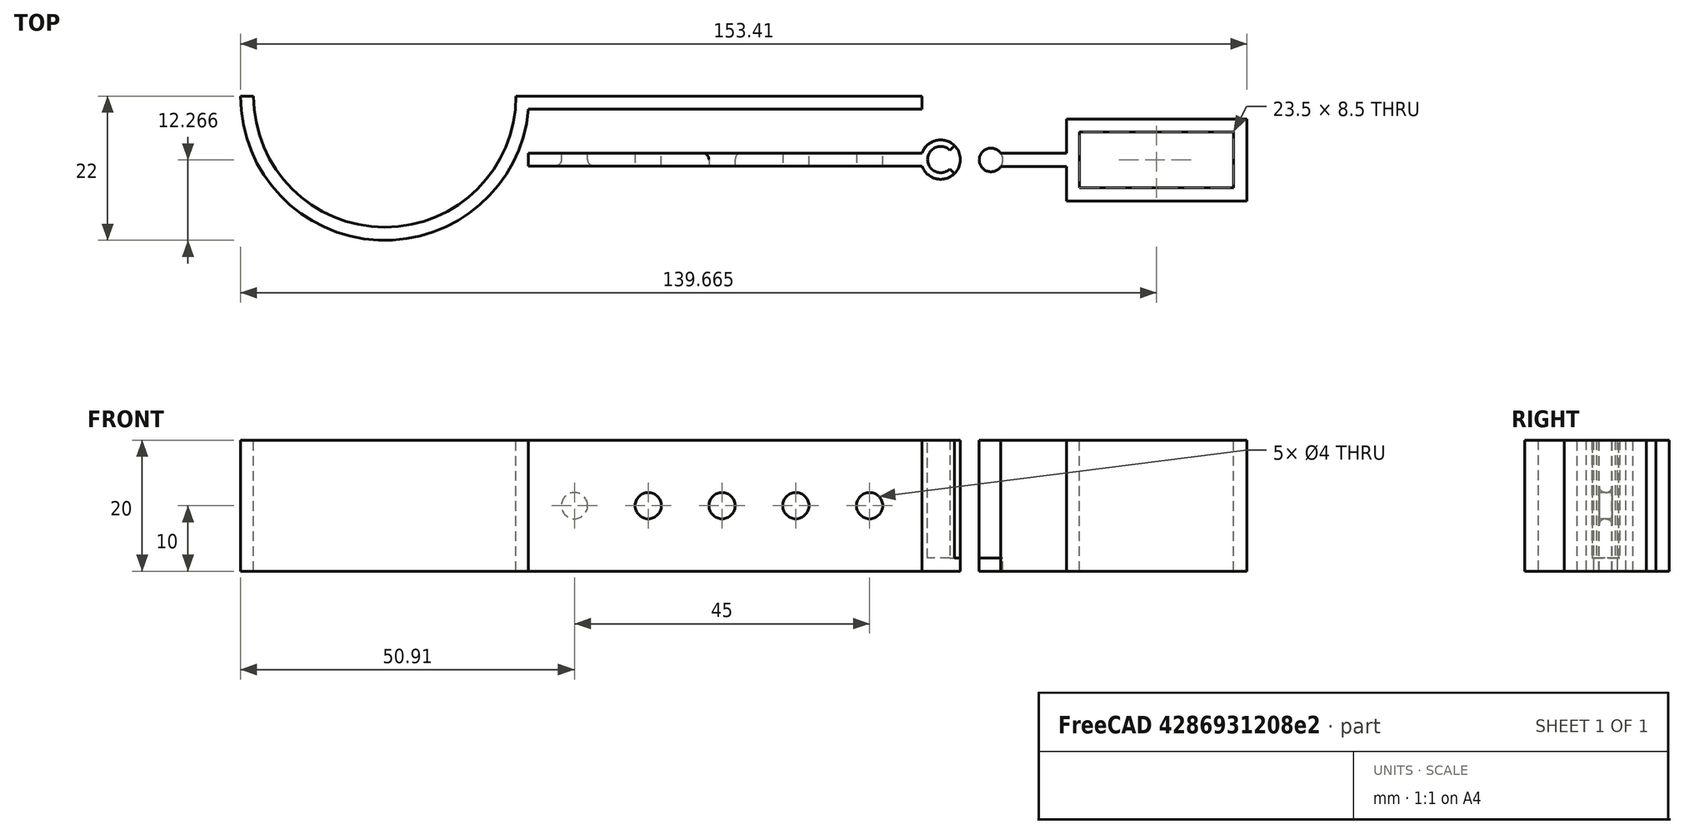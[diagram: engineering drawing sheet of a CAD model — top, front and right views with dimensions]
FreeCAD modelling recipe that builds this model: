
FCSTD DOCUMENT  (FreeCAD 0.16R6712 (Git))
Label: Porte webcam
License: All rights reserved
LicenseURL: http://en.wikipedia.org/wiki/All_rights_reserved
objects: Sketcher::SketchObject×7, PartDesign::Pocket×4, PartDesign::Pad×3, Mesh::Feature×3, PartDesign::LinearPattern×2, PartDesign::Fillet×2
note: 25 computed .brp shape members not serialized (recipe doc carries the construction recipe); baked Part::Feature solids carry a one-line shape summary decoded from their .brp

FEATURE [Sketcher::SketchObject] Sketch
  sketch-geometry (6):
    g0: ArcOfCircle CenterX=-81.9089 CenterY=0 CenterZ=0 NormalX=0 NormalY=0 NormalZ=1 Radius=20 StartAngle=3.14159 EndAngle=6.28319
    g1: ArcOfCircle CenterX=-81.9089 CenterY=0 CenterZ=0 NormalX=0 NormalY=0 NormalZ=1 Radius=22 StartAngle=3.14159 EndAngle=6.19215
    g2: LineSegment StartX=-60 StartY=-2 StartZ=0 EndX=0 EndY=-2 EndZ=0
    g3: LineSegment StartX=-61.9089 StartY=0 StartZ=0 EndX=0 EndY=0 EndZ=0
    g4: LineSegment StartX=0 StartY=-2 StartZ=0 EndX=0 EndY=0 EndZ=0
    g5: LineSegment StartX=-103.909 StartY=0 StartZ=0 EndX=-101.909 EndY=0 EndZ=0
  constraints (18):
    c: PointOnObject(g0,g-1)
    c: PointOnObject(g0,g-1)
    c: PointOnObject(g0,g-1)
    c: Radius(g0) = 20
    c: Coincident(g1,g0)
    c: PointOnObject(g1,g-1)
    c: DistanceX(g1,g0) = 2
    c: Coincident(g2,g1)
    c: Horizontal(g2)
    c: Coincident(g3,g-1)
    c: DistanceY(g2,g-1) = 2
    c: Coincident(g4,g-1)
    c: Vertical(g4)
    c: Coincident(g2,g4)
    c: Coincident(g3,g0)
    c: Coincident(g5,g1)
    c: Coincident(g5,g0)
    c: DistanceX(g1,g2) = 60
FEATURE [PartDesign::Pad] Pad
  Length = 20
  Length2 = 100
  Sketch = -> Sketch
  Type = 0
FEATURE [Sketcher::SketchObject] Sketch001
  ExternalGeometry = -> [Pad]
  Placement = pos=(0,-2,0) rot=(1,0,0;1.5708rad)
  Support = -> Pad [Face5]
  sketch-geometry (3):
    g0: Circle CenterX=-53 CenterY=10 CenterZ=0 NormalX=0 NormalY=0 NormalZ=1 Radius=2
    g1: LineSegment [constr] StartX=-53 StartY=10 StartZ=0 EndX=-53 EndY=20 EndZ=0
    g2: LineSegment [constr] StartX=-53 StartY=10 StartZ=0 EndX=-53 EndY=0 EndZ=0
  constraints (9):
    c: Radius(g0) = 2
    c: DistanceX(g-3,g0) = 7
    c: Coincident(g1,g0)
    c: Vertical(g1)
    c: Coincident(g2,g0)
    c: PointOnObject(g2,g-4)
    c: Vertical(g2)
    c: PointOnObject(g1,g-3)
    c: Equal(g1,g2)
FEATURE [PartDesign::Pocket] Pocket
  Length = 5
  Sketch = -> Sketch001
  Type = 1
FEATURE [Sketcher::SketchObject] Sketch002
  sketch-geometry (4):
    g0: LineSegment StartX=0 StartY=-8.67651 StartZ=0 EndX=-60 EndY=-8.67651 EndZ=0
    g1: LineSegment StartX=-60 StartY=-8.67651 StartZ=0 EndX=-60 EndY=-10.6765 EndZ=0
    g2: LineSegment StartX=-60 StartY=-10.6765 StartZ=0 EndX=0 EndY=-10.6765 EndZ=0
    g3: ArcOfCircle CenterX=2.82843 CenterY=-9.67651 CenterZ=0 NormalX=0 NormalY=0 NormalZ=1 Radius=3 StartAngle=3.48143 EndAngle=9.08494
  constraints (12):
    c: PointOnObject(g0,g-2)
    c: Horizontal(g0)
    c: Coincident(g0,g1)
    c: Vertical(g1)
    c: Coincident(g1,g2)
    c: PointOnObject(g2,g-2)
    c: Horizontal(g2)
    c: DistanceY(g1,g0) = 2
    c: DistanceX(g1,g2) = 60
    c: Coincident(g3,g0)
    c: Coincident(g3,g2)
    c: Radius(g3) = 3
FEATURE [PartDesign::Pad] Pad001
  Length = 20
  Length2 = 100
  Sketch = -> Sketch002
  Type = 0
FEATURE [Sketcher::SketchObject] Sketch003
  ExternalGeometry = -> [Pad001]
  Placement = pos=(0,-10.6765,0) rot=(1,0,0;1.5708rad)
  Support = -> Pad001 [Face3]
  sketch-geometry (3):
    g0: LineSegment [constr] StartX=-53 StartY=10 StartZ=0 EndX=-53 EndY=20 EndZ=0
    g1: LineSegment [constr] StartX=-53 StartY=10 StartZ=0 EndX=-53 EndY=0 EndZ=0
    g2: Circle CenterX=-53 CenterY=10 CenterZ=0 NormalX=0 NormalY=0 NormalZ=1 Radius=2
  constraints (9):
    c: PointOnObject(g0,g-3)
    c: Vertical(g0)
    c: PointOnObject(g1,g-4)
    c: Vertical(g1)
    c: Equal(g1,g0)
    c: Radius(g2) = 2
    c: Coincident(g1,g2)
    c: Coincident(g1,g0)
    c: DistanceX(g-3,g0) = 7
FEATURE [PartDesign::Pocket] Pocket001
  Length = 5
  Sketch = -> Sketch003
  Type = 1
FEATURE [Sketcher::SketchObject] Sketch004
  sketch-geometry (14):
    g0: LineSegment StartX=24.0046 StartY=-5.48438 StartZ=0 EndX=47.5046 EndY=-5.48438 EndZ=0
    g1: LineSegment StartX=47.5046 StartY=-5.48438 StartZ=0 EndX=47.5046 EndY=-13.9844 EndZ=0
    g2: LineSegment StartX=47.5046 StartY=-13.9844 StartZ=0 EndX=24.0046 EndY=-13.9844 EndZ=0
    g3: LineSegment StartX=24.0046 StartY=-13.9844 StartZ=0 EndX=24.0046 EndY=-5.48438 EndZ=0
    g4: LineSegment StartX=22.0046 StartY=-3.48438 StartZ=0 EndX=49.5046 EndY=-3.48438 EndZ=0
    g5: LineSegment StartX=49.5046 StartY=-3.48438 StartZ=0 EndX=49.5046 EndY=-15.9844 EndZ=0
    g6: LineSegment StartX=49.5046 StartY=-15.9844 StartZ=0 EndX=22.0046 EndY=-15.9844 EndZ=0
    g7: LineSegment StartX=12.0046 StartY=-8.73438 StartZ=0 EndX=22.0046 EndY=-8.73438 EndZ=0
    g8: LineSegment StartX=22.0046 StartY=-10.7344 StartZ=0 EndX=12.0046 EndY=-10.7344 EndZ=0
    g9: LineSegment StartX=22.0046 StartY=-15.9844 StartZ=0 EndX=22.0046 EndY=-10.7344 EndZ=0
    g10: LineSegment StartX=22.0046 StartY=-8.73438 StartZ=0 EndX=22.0046 EndY=-3.48438 EndZ=0
    g11: ArcOfCircle CenterX=10.508 CenterY=-9.73438 CenterZ=0 NormalX=0 NormalY=0 NormalZ=1 Radius=1.8 StartAngle=0.589031 EndAngle=5.69415
    g12: LineSegment [constr] StartX=12.0046 StartY=-10.7344 StartZ=0 EndX=10.508 EndY=-9.73438 EndZ=0
    g13: LineSegment [constr] StartX=10.508 StartY=-9.73438 StartZ=0 EndX=12.0046 EndY=-8.73438 EndZ=0
  constraints (39):
    c: Coincident(g0,g1)
    c: Coincident(g1,g2)
    c: Coincident(g2,g3)
    c: Coincident(g3,g0)
    c: Horizontal(g0)
    c: Horizontal(g2)
    c: Vertical(g1)
    c: Vertical(g3)
    c: Coincident(g4,g5)
    c: Coincident(g5,g6)
    c: Horizontal(g4)
    c: Horizontal(g6)
    c: Vertical(g5)
    c: DistanceY(g5,g1) = 2
    c: DistanceX(g1,g5) = 2
    c: DistanceX(g4,g0) = 2
    c: DistanceY(g0,g4) = 2
    c: DistanceX(g0,g0) = 23.5
    c: DistanceY(g2,g0) = 8.5
    c: Horizontal(g7)
    c: Horizontal(g8)
    c: DistanceY(g8,g7) = 2
    c: Coincident(g9,g6)
    c: Vertical(g9)
    c: Coincident(g10,g7)
    c: Coincident(g10,g4)
    c: Vertical(g10)
    c: Equal(g9,g10)
    c: Coincident(g9,g8)
    c: DistanceX(g6,g2) = 2
    c: DistanceX(g8,g8) = 10
    c: Coincident(g11,g7)
    c: Coincident(g11,g8)
    c: Radius(g11) = 1.8
    c: Coincident(g12,g8)
    c: Coincident(g12,g11)
    c: Coincident(g13,g11)
    c: Coincident(g13,g7)
    c: Equal(g8,g7)
FEATURE [PartDesign::LinearPattern] LinearPattern
  Direction = -> Sketch001 [H_Axis]
  Length = 45
  Occurrences = 5
  Originals = -> [Pocket]
FEATURE [PartDesign::Pad] Pad002
  Length = 20
  Length2 = 100
  Sketch = -> Sketch004
  Type = 0
FEATURE [PartDesign::LinearPattern] LinearPattern001
  Direction = -> Sketch003 [H_Axis]
  Length = 45
  Occurrences = 5
  Originals = -> [Pocket001]
FEATURE [Sketcher::SketchObject] Sketch005
  ExternalGeometry = -> [LinearPattern001]
  Placement = pos=(0,0,20) rot=(0,0,1;0rad)
  Support = -> LinearPattern001 [Face4]
  sketch-geometry (5):
    g0: ArcOfCircle CenterX=2.82843 CenterY=-9.67651 CenterZ=0 NormalX=0 NormalY=0 NormalZ=1 Radius=3.81642 StartAngle=5.49779 EndAngle=7.06858
    g1: LineSegment [constr] StartX=2.82843 StartY=-9.67651 StartZ=0 EndX=7.82755 EndY=-9.67651 EndZ=0
    g2: ArcOfCircle CenterX=2.82843 CenterY=-9.67651 CenterZ=0 NormalX=0 NormalY=0 NormalZ=1 Radius=2 StartAngle=0.785398 EndAngle=5.49779
    g3: LineSegment StartX=4.24264 StartY=-8.26229 StartZ=0 EndX=5.52704 EndY=-6.97789 EndZ=0
    g4: LineSegment StartX=4.24264 StartY=-11.0907 StartZ=0 EndX=5.52704 EndY=-12.3751 EndZ=0
  constraints (13):
    c: Angle(g0) = 1.5708
    c: Horizontal(g1)
    c: Symmetric(g0,g0,g1)
    c: Coincident(g2,g0)
    c: Radius(g2) = 2
    c: Coincident(g3,g2)
    c: Coincident(g3,g0)
    c: Coincident(g4,g2)
    c: Coincident(g4,g0)
    c: Coincident(g-3,g1)
    c: Coincident(g0,g1)
    c: Symmetric(g2,g2,g1)
    c: Angle(g2) = 4.71239
FEATURE [PartDesign::Pocket] Pocket002
  Length = 18
  Sketch = -> Sketch005
  Type = 0
FEATURE [Sketcher::SketchObject] Sketch006
  ExternalGeometry = -> [Pad002]
  Placement = pos=(0,0,0) rot=(1,0,0;3.14159rad)
  Support = -> Pad002 [Face13]
  sketch-geometry (4):
    g0: Circle CenterX=10.508 CenterY=9.73438 CenterZ=0 NormalX=0 NormalY=0 NormalZ=1 Radius=1.8
    g1: LineSegment [constr] StartX=12.0046 StartY=10.7344 StartZ=0 EndX=10.508 EndY=9.73438 EndZ=0
    g2: GeomPoint [constr] X=12.2971 Y=9.53666 Z=0
    g3: LineSegment [constr] StartX=10.508 StartY=9.73438 StartZ=0 EndX=12.2971 EndY=9.53666 EndZ=0
  constraints (7):
    c: Coincident(g0,g-3)
    c: Coincident(g1,g-3)
    c: Coincident(g1,g0)
    c: PointOnObject(g2,g0)
    c: Coincident(g3,g0)
    c: Coincident(g3,g2)
    c: Equal(g1,g3)
FEATURE [PartDesign::Pocket] Pocket003
  Length = 2
  Sketch = -> Sketch006
  Type = 0
FEATURE [PartDesign::Fillet] Fillet
  Base = -> Pocket002 [Edge33]
  Radius = 1
FEATURE [PartDesign::Fillet] Fillet001
  Base = -> Fillet [Edge11]
  Radius = 1
FEATURE [Mesh::Feature] Mesh  label="Support tube"
FEATURE [Mesh::Feature] Mesh001  label="Bras"
FEATURE [Mesh::Feature] Mesh002  label="Support webcam"
